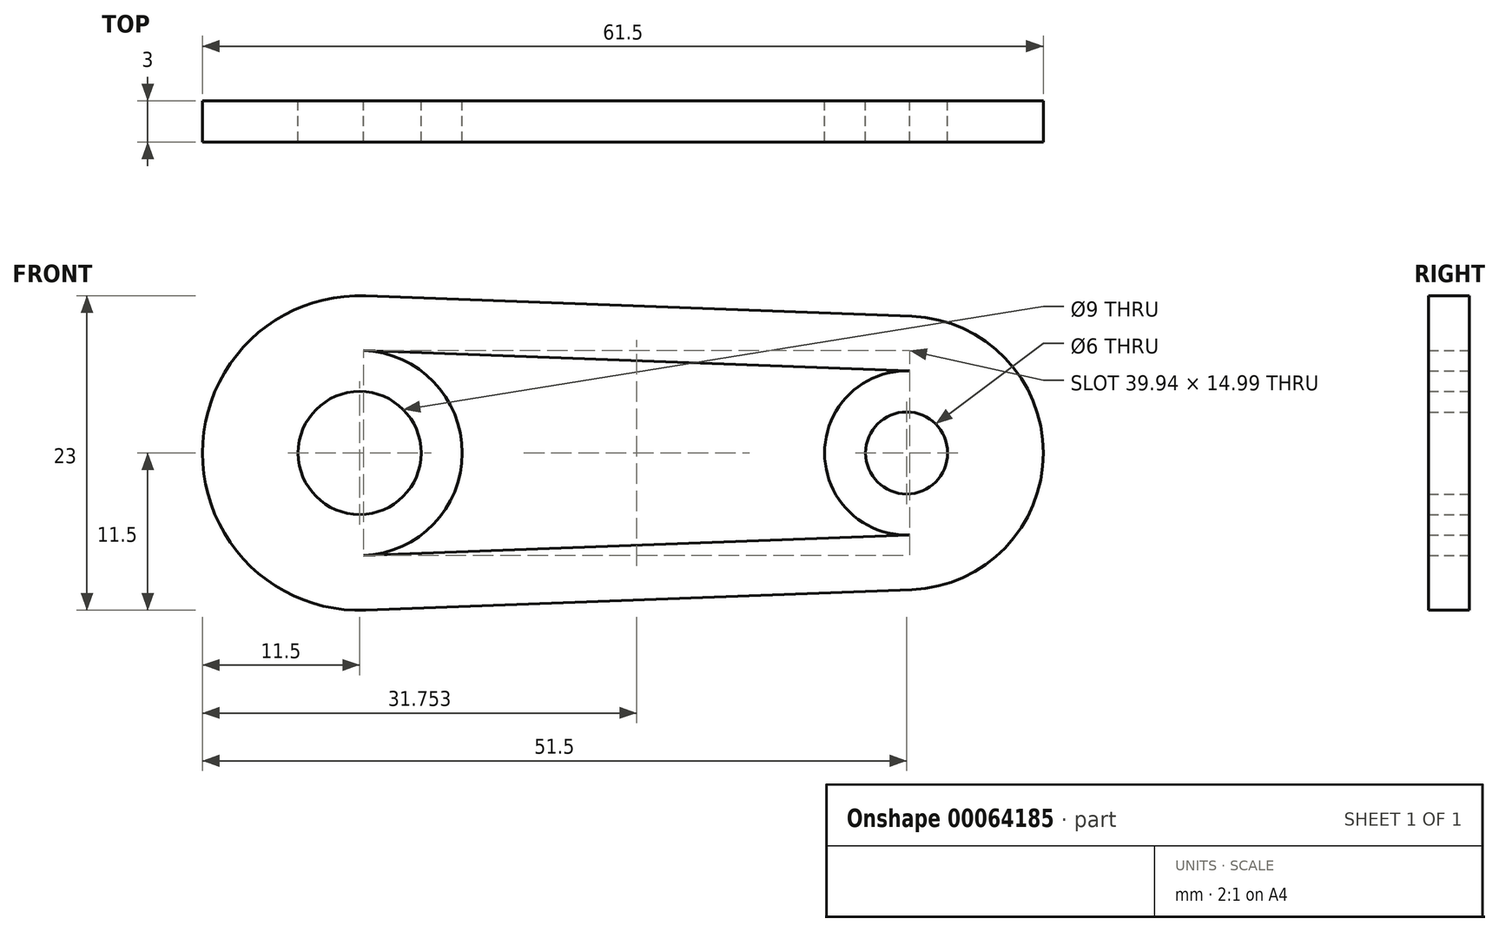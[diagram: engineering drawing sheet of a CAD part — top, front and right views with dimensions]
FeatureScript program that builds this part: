
annotation { "Feature Type Name" : "Feature", "Feature Type Description" : "" }
export const myFeature = defineFeature(function(context is Context, id is Id, definition is map)
    precondition{}
    {
        {
            var Q0;
            Q0=qCreatedBy(makeId("Front.planeOp"),FACE);
            var sketch = newSketch(context, id + "F0", { "sketchPlane" : qUnion([Q0])});
            skArc(sketch, "E0", {"start": v(0.28, 7.5) * mm, "mid": v(-7.5, 0) * mm, "end": v(0.28, -7.5) * mm});
            skArc(sketch, "E1", {"start": v(40.23, -6) * mm, "mid": v(46, 0) * mm, "end": v(40.23, 6) * mm});
            skLineSegment(sketch, "E2", {"start": v(0.28, 7.5) * mm, "end": v(40.23, 6) * mm});
            skLineSegment(sketch, "E3.MirrorCS", {"start": v(0.28, -7.5) * mm, "end": v(40.23, -6) * mm});
            skLineSegment(sketch, "E4.0", {"start": v(0.43, 11.5) * mm, "end": v(40.38, 10) * mm});
            skArc(sketch, "E4.1", {"start": v(0.43, 11.5) * mm, "mid": v(-11.5, 0) * mm, "end": v(0.43, -11.5) * mm});
            skLineSegment(sketch, "E4.2", {"start": v(0.43, -11.5) * mm, "end": v(40.38, -10) * mm});
            skArc(sketch, "E4.3", {"start": v(40.38, -10) * mm, "mid": v(50, 0) * mm, "end": v(40.38, 10) * mm});
            skCircle(sketch, "E5", {"center": v(0, 0) * mm, "radius": 7.5 * mm});
            skCircle(sketch, "E6", {"center": v(40, 0) * mm, "radius": 6 * mm});
            skCircle(sketch, "E7.0", {"center": v(0, 0) * mm, "radius": 4.5 * mm});
            skCircle(sketch, "E8.0", {"center": v(40, 0) * mm, "radius": 3 * mm});
            skSolve(sketch);
        }
        {
            var Q0;
            Q0 = qSketchRegion(id + "F0", true);
            var Q1;
            {var subQ0=sQuery(id+"F0.wireOp",EDGE,"E5");var subQ1=makeQuery(id+"F0.imprint","INTERSECT",VERTEX,{"derivedFrom":[sQuery(id+"F0.wireOp",EDGE,"E2"),subQ0]});Q1=makeQuery(id+"F0.imprint","IMPRINT",FACE,{"disambiguationData":[TD([[makeQuery(id+"F0.imprint","IMPRINT",EDGE,{"disambiguationData":[TD([[subQ1,-1.0]])],"derivedFrom":subQ0}),1.0]])]});}
            var Q2;
            {var subQ0=sQuery(id+"F0.wireOp",EDGE,"E6");var subQ1=makeQuery(id+"F0.imprint","INTERSECT",VERTEX,{"derivedFrom":[sQuery(id+"F0.wireOp",EDGE,"E2"),subQ0]});Q2=makeQuery(id+"F0.imprint","IMPRINT",FACE,{"disambiguationData":[TD([[makeQuery(id+"F0.imprint","IMPRINT",EDGE,{"disambiguationData":[TD([[subQ1,-1.0]])],"derivedFrom":subQ0}),1.0]])]});}
            extrude(context, id + "F1", {"entities" : qUnion([Q0, Q1, Q2]), "depth" : 3 * mm});
        }
    });
